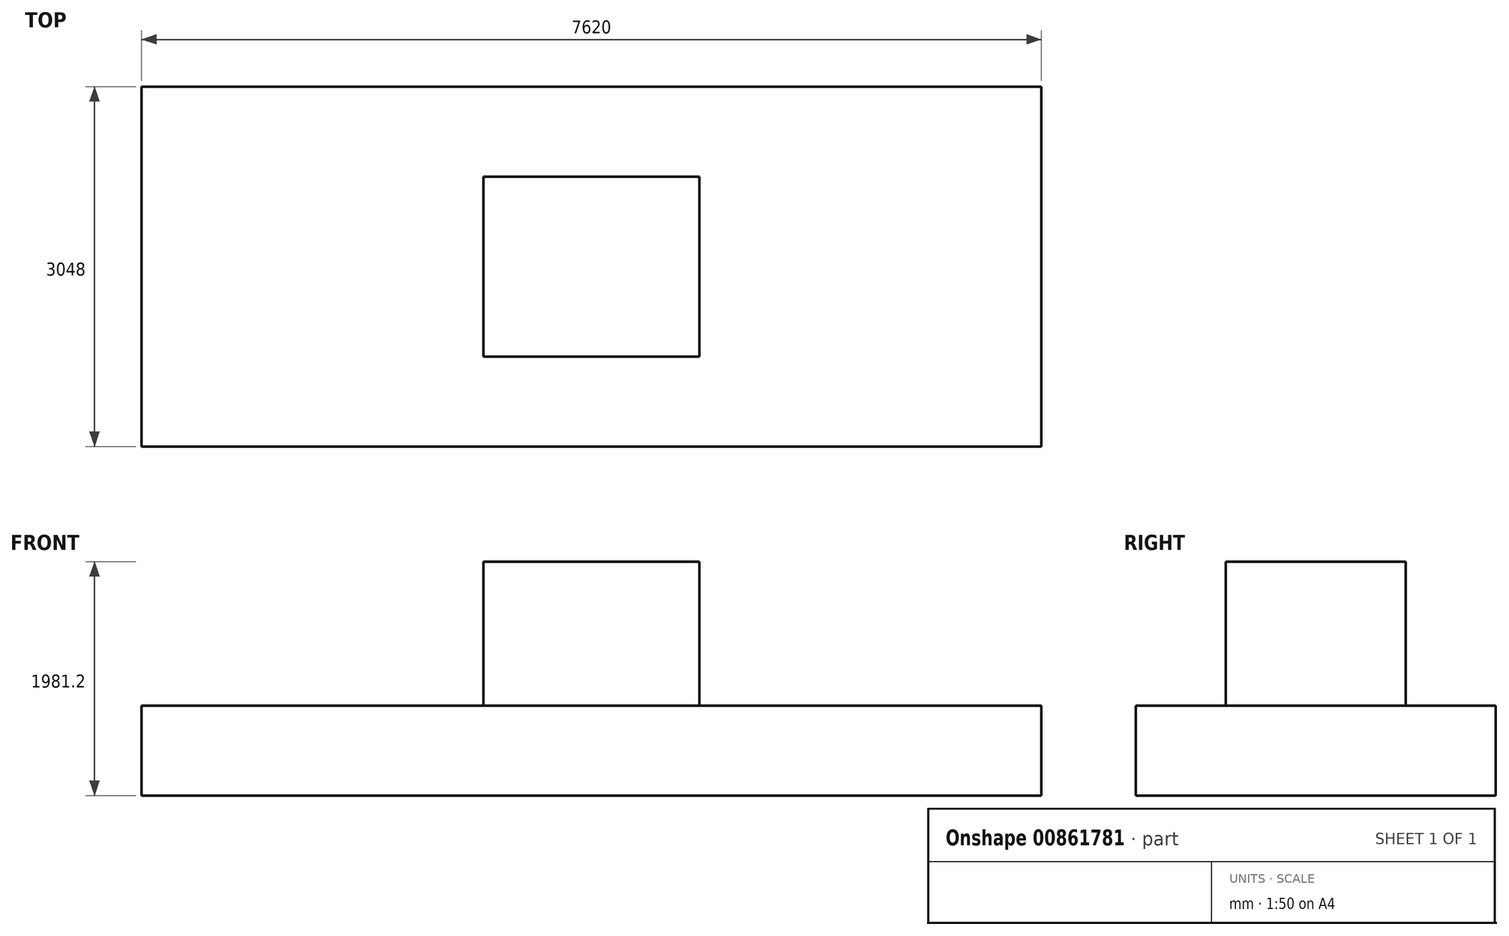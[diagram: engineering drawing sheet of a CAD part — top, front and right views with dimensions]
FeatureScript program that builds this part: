
annotation { "Feature Type Name" : "Feature", "Feature Type Description" : "" }
export const myFeature = defineFeature(function(context is Context, id is Id, definition is map)
    precondition{}
    {
        {
            var Q0;
            Q0=qCreatedBy(makeId("Top.planeOp"),FACE);
            var sketch = newSketch(context, id + "F0", { "sketchPlane" : qUnion([Q0])});
            skLineSegment(sketch, "E0.bottom", {"start": v(3810, 1524) * mm, "end": v(-3810, 1524) * mm});
            skLineSegment(sketch, "E0.top", {"start": v(3810, -1524) * mm, "end": v(-3810, -1524) * mm});
            skLineSegment(sketch, "E0.left", {"start": v(3810, 1524) * mm, "end": v(3810, -1524) * mm});
            skLineSegment(sketch, "E0.right", {"start": v(-3810, 1524) * mm, "end": v(-3810, -1524) * mm});
            skPoint(sketch, "E0.middle", {"position": v(0, 0) * mm});
            skSolve(sketch);
        }
        {
            var Q0;
            Q0=makeQuery(id+"F0.imprint","IMPRINT",FACE,{"disambiguationData":[TD([[makeQuery(id+"F0.imprint","IMPRINT",EDGE,{"derivedFrom":sQuery(id+"F0.wireOp",EDGE,"E0.bottom")}),1.0]])]});
            extrude(context, id + "F1", {"entities" : qUnion([Q0]), "depth" : 762 * mm, "offsetDistance" : 25.4 * mm});
        }
        {
            var Q0;
            Q0=makeQuery(id+"F1.opExtrude","CAP_FACE",FACE,{"disambiguationData":[OSD([sQuery(id+"F0.wireOp",EDGE,"E0.bottom"),sQuery(id+"F0.wireOp",EDGE,"E0.top"),sQuery(id+"F0.wireOp",EDGE,"E0.left"),sQuery(id+"F0.wireOp",EDGE,"E0.right")])],"isStart":false});
            var sketch = newSketch(context, id + "F2", { "sketchPlane" : qUnion([Q0])});
            skLineSegment(sketch, "E1.bottom", {"start": v(914.4, -762) * mm, "end": v(-914.4, -762) * mm});
            skLineSegment(sketch, "E1.top", {"start": v(914.4, 762) * mm, "end": v(-914.4, 762) * mm});
            skLineSegment(sketch, "E1.left", {"start": v(914.4, -762) * mm, "end": v(914.4, 762) * mm});
            skLineSegment(sketch, "E1.right", {"start": v(-914.4, -762) * mm, "end": v(-914.4, 762) * mm});
            skPoint(sketch, "E1.middle", {"position": v(0, 0) * mm});
            skSolve(sketch);
        }
        {
            var Q0;
            Q0 = qSketchRegion(id + "F2", true);
            extrude(context, id + "F3", {"entities" : qUnion([Q0]), "depth" : 1219.2 * mm, "offsetDistance" : 25.4 * mm});
        }
    });
